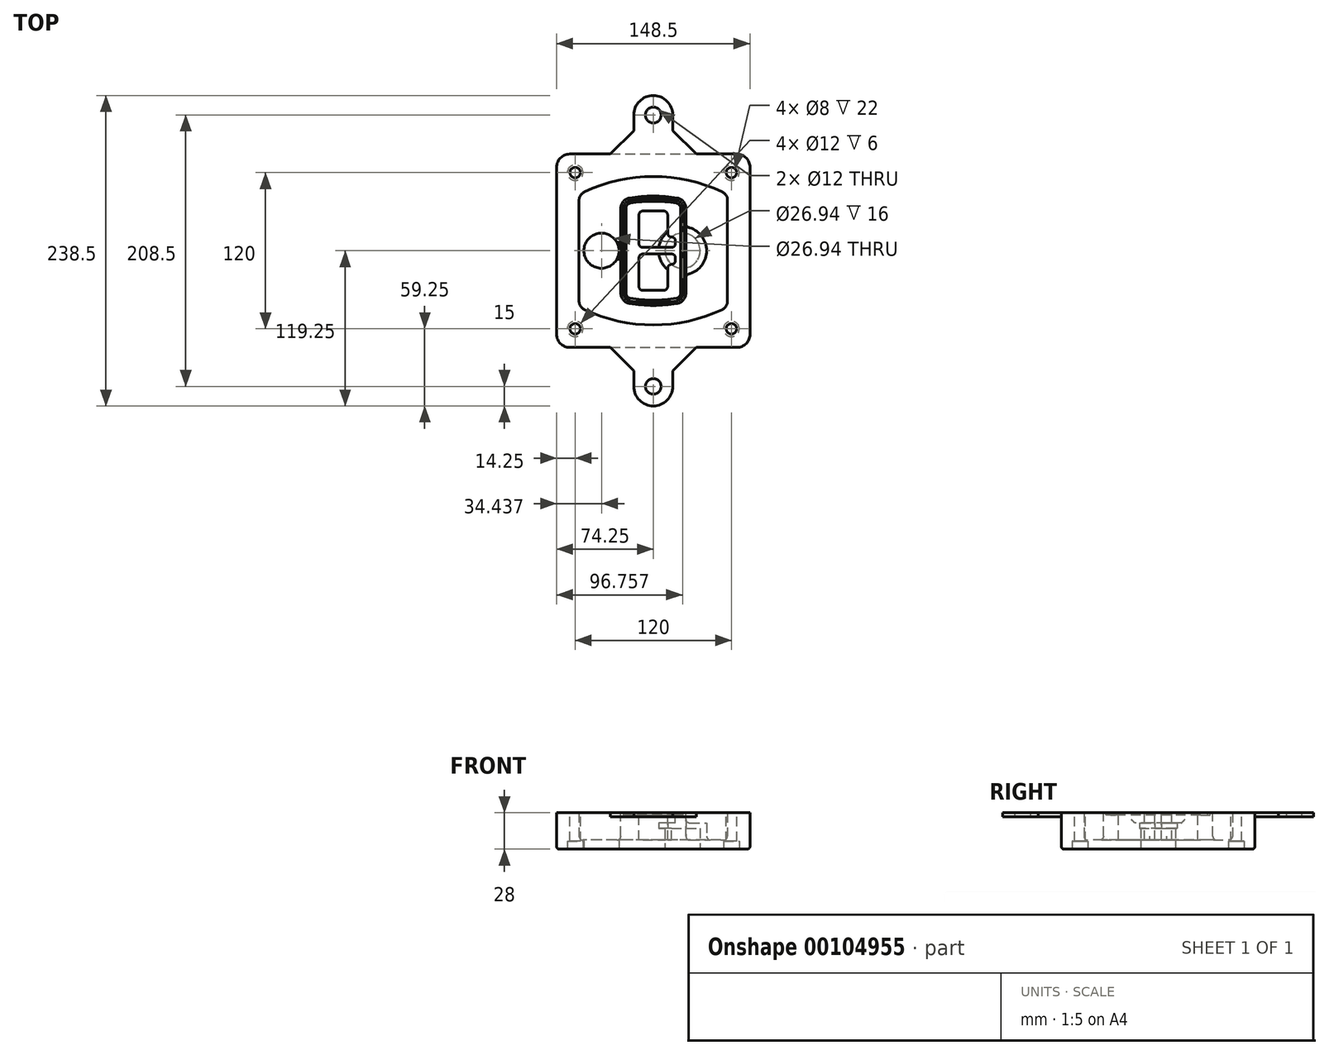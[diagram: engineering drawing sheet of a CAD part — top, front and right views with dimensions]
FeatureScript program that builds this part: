
annotation { "Feature Type Name" : "Feature", "Feature Type Description" : "" }
export const myFeature = defineFeature(function(context is Context, id is Id, definition is map)
    precondition{}
    {
        {
            var Q0;
            Q0=qCreatedBy(makeId("Top.planeOp"),FACE);
            var sketch = newSketch(context, id + "F0", { "sketchPlane" : qUnion([Q0])});
            skPoint(sketch, "E0.rect.middle", {"position": v(0, 0) * mm});
            skLineSegment(sketch, "E1.bottom", {"start": v(-64.25, -74.25) * mm, "end": v(64.25, -74.25) * mm});
            skLineSegment(sketch, "E1.top", {"start": v(-64.25, 74.25) * mm, "end": v(64.25, 74.25) * mm});
            skLineSegment(sketch, "E1.left", {"start": v(-74.25, -64.25) * mm, "end": v(-74.25, 64.25) * mm});
            skLineSegment(sketch, "E1.right", {"start": v(74.25, -64.25) * mm, "end": v(74.25, 64.25) * mm});
            skLineSegment(sketch, "E2", {"start": v(-74.25, 74.25) * mm, "end": v(74.25, -74.25) * mm, "construction": true});
            skLineSegment(sketch, "E3", {"start": v(74.25, 74.25) * mm, "end": v(-74.25, -74.25) * mm, "construction": true});
            skCircle(sketch, "E4", {"center": v(-60, 60) * mm, "radius": 4 * mm});
            skCircle(sketch, "E5", {"center": v(60, 60) * mm, "radius": 4 * mm});
            skCircle(sketch, "E6", {"center": v(60, -60) * mm, "radius": 4 * mm});
            skCircle(sketch, "E7", {"center": v(-60, -60) * mm, "radius": 4 * mm});
            skLineSegment(sketch, "E8", {"start": v(-60, 60) * mm, "end": v(60, 60) * mm, "construction": true});
            skLineSegment(sketch, "E9", {"start": v(60, 60) * mm, "end": v(60, -60) * mm, "construction": true});
            skLineSegment(sketch, "E10", {"start": v(60, -60) * mm, "end": v(-60, -60) * mm, "construction": true});
            skLineSegment(sketch, "E11", {"start": v(-60, -60) * mm, "end": v(-60, 60) * mm, "construction": true});
            skLineSegment(sketch, "E12", {"start": v(-60, 38.83) * mm, "end": v(-60, -38.83) * mm});
            skLineSegment(sketch, "E13", {"start": v(60, 38.83) * mm, "end": v(60, -38.83) * mm});
            skArc(sketch, "E14", {"start": v(54.26, 47.88) * mm, "mid": v(0, 60) * mm, "end": v(-54.26, 47.88) * mm});
            skArc(sketch, "E15", {"start": v(-54.26, -47.88) * mm, "mid": v(0, -60) * mm, "end": v(54.26, -47.88) * mm});
            skLineSegment(sketch, "E16", {"start": v(-60, 0) * mm, "end": v(60, 0) * mm, "construction": true});
            skPoint(sketch, "E17.visualSharp", {"position": v(-60, -45) * mm});
            skArc(sketch, "E17.filletArc", {"start": v(-60, -38.83) * mm, "mid": v(-58.44, -44.2) * mm, "end": v(-54.26, -47.88) * mm});
            skPoint(sketch, "E18.visualSharp", {"position": v(-60, 45) * mm});
            skArc(sketch, "E18.filletArc", {"start": v(-54.26, 47.88) * mm, "mid": v(-58.44, 44.2) * mm, "end": v(-60, 38.83) * mm});
            skPoint(sketch, "E19.visualSharp", {"position": v(60, 45) * mm});
            skArc(sketch, "E19.filletArc", {"start": v(60, 38.83) * mm, "mid": v(58.44, 44.2) * mm, "end": v(54.26, 47.88) * mm});
            skPoint(sketch, "E20.visualSharp", {"position": v(60, -45) * mm});
            skArc(sketch, "E20.filletArc", {"start": v(54.26, -47.88) * mm, "mid": v(58.44, -44.2) * mm, "end": v(60, -38.83) * mm});
            skPoint(sketch, "E21.visualSharp", {"position": v(-74.25, 74.25) * mm});
            skArc(sketch, "E21.filletArc", {"start": v(-64.25, 74.25) * mm, "mid": v(-71.32, 71.32) * mm, "end": v(-74.25, 64.25) * mm});
            skPoint(sketch, "E22.visualSharp", {"position": v(74.25, 74.25) * mm});
            skArc(sketch, "E22.filletArc", {"start": v(74.25, 64.25) * mm, "mid": v(71.32, 71.32) * mm, "end": v(64.25, 74.25) * mm});
            skPoint(sketch, "E23.visualSharp", {"position": v(74.25, -74.25) * mm});
            skArc(sketch, "E23.filletArc", {"start": v(64.25, -74.25) * mm, "mid": v(71.32, -71.32) * mm, "end": v(74.25, -64.25) * mm});
            skPoint(sketch, "E24.visualSharp", {"position": v(-74.25, -74.25) * mm});
            skArc(sketch, "E24.filletArc", {"start": v(-74.25, -64.25) * mm, "mid": v(-71.32, -71.32) * mm, "end": v(-64.25, -74.25) * mm});
            skArc(sketch, "E25.0", {"start": v(57, 38.83) * mm, "mid": v(55.9, 42.58) * mm, "end": v(52.98, 45.17) * mm});
            skLineSegment(sketch, "E25.1", {"start": v(57, 38.83) * mm, "end": v(57, -38.83) * mm});
            skArc(sketch, "E25.2", {"start": v(52.98, -45.17) * mm, "mid": v(55.9, -42.58) * mm, "end": v(57, -38.83) * mm});
            skArc(sketch, "E25.3", {"start": v(-52.98, -45.17) * mm, "mid": v(0, -57) * mm, "end": v(52.98, -45.17) * mm});
            skArc(sketch, "E25.4", {"start": v(-57, -38.83) * mm, "mid": v(-55.9, -42.58) * mm, "end": v(-52.98, -45.17) * mm});
            skArc(sketch, "E25.5", {"start": v(52.98, 45.17) * mm, "mid": v(0, 57) * mm, "end": v(-52.98, 45.17) * mm});
            skLineSegment(sketch, "E25.6", {"start": v(-57, 38.83) * mm, "end": v(-57, -38.83) * mm});
            skArc(sketch, "E25.7", {"start": v(-52.98, 45.17) * mm, "mid": v(-55.9, 42.58) * mm, "end": v(-57, 38.83) * mm});
            skArc(sketch, "E26.0", {"start": v(-55.96, 51.5) * mm, "mid": v(-61.82, 46.33) * mm, "end": v(-64, 38.83) * mm});
            skArc(sketch, "E26.1", {"start": v(55.96, 51.5) * mm, "mid": v(0, 64) * mm, "end": v(-55.96, 51.5) * mm});
            skArc(sketch, "E26.2", {"start": v(64, 38.83) * mm, "mid": v(61.82, 46.33) * mm, "end": v(55.96, 51.5) * mm});
            skLineSegment(sketch, "E26.3", {"start": v(64, 38.83) * mm, "end": v(64, -38.83) * mm});
            skArc(sketch, "E26.4", {"start": v(55.96, -51.5) * mm, "mid": v(61.82, -46.33) * mm, "end": v(64, -38.83) * mm});
            skLineSegment(sketch, "E26.5", {"start": v(-64, 38.83) * mm, "end": v(-64, -38.83) * mm});
            skArc(sketch, "E26.6", {"start": v(-55.96, -51.5) * mm, "mid": v(0, -64) * mm, "end": v(55.96, -51.5) * mm});
            skArc(sketch, "E26.7", {"start": v(-64, -38.83) * mm, "mid": v(-61.82, -46.33) * mm, "end": v(-55.96, -51.5) * mm});
            skSolve(sketch);
        }
        {
            var Q0;
            Q0=makeQuery(id+"F0.imprint","IMPRINT",FACE,{"disambiguationData":[TD([[makeQuery(id+"F0.imprint","IMPRINT",EDGE,{"derivedFrom":sQuery(id+"F0.wireOp",EDGE,"E1.bottom")}),1.0]])]});
            var Q1;
            Q1=makeQuery(id+"F0.imprint","IMPRINT",FACE,{"disambiguationData":[TD([[makeQuery(id+"F0.imprint","IMPRINT",EDGE,{"derivedFrom":sQuery(id+"F0.wireOp",EDGE,"E12")}),1.0]])]});
            var Q2;
            Q2=makeQuery(id+"F0.imprint","IMPRINT",FACE,{"disambiguationData":[TD([[makeQuery(id+"F0.imprint","IMPRINT",EDGE,{"derivedFrom":sQuery(id+"F0.wireOp",EDGE,"E25.0")}),1.0]])]});
            var Q3;
            Q3=makeQuery(id+"F0.imprint","IMPRINT",FACE,{"disambiguationData":[TD([[makeQuery(id+"F0.imprint","IMPRINT",EDGE,{"derivedFrom":sQuery(id+"F0.wireOp",EDGE,"E12")}),-1.0]])]});
            extrude(context, id + "F1", {"entities" : qUnion([Q0, Q1, Q2, Q3]), "oppositeDirection" : true, "depth" : 25 * mm});
        }
        {
            var Q0;
            Q0=makeQuery(id+"F0.imprint","IMPRINT",FACE,{"disambiguationData":[TD([[makeQuery(id+"F0.imprint","IMPRINT",EDGE,{"derivedFrom":sQuery(id+"F0.wireOp",EDGE,"E12")}),1.0]])]});
            extrude(context, id + "F2", {"entities" : qUnion([Q0]), "operationType" : NewBodyOperationType.ADD, "depth" : 3 * mm});
        }
        {
            var Q0;
            Q0=makeQuery(id+"F0.imprint","IMPRINT",FACE,{"disambiguationData":[TD([[makeQuery(id+"F0.imprint","IMPRINT",EDGE,{"derivedFrom":sQuery(id+"F0.wireOp",EDGE,"E25.0")}),1.0]])]});
            extrude(context, id + "F3", {"entities" : qUnion([Q0]), "operationType" : NewBodyOperationType.REMOVE, "oppositeDirection" : true, "depth" : 18 * mm});
        }
        {
            var Q0;
            Q0=makeQuery(id+"F2.opExtrude","CAP_FACE",FACE,{"disambiguationData":[OSD([sQuery(id+"F0.wireOp",EDGE,"E12"),sQuery(id+"F0.wireOp",EDGE,"E13"),sQuery(id+"F0.wireOp",EDGE,"E14"),sQuery(id+"F0.wireOp",EDGE,"E15"),sQuery(id+"F0.wireOp",EDGE,"E17.filletArc"),sQuery(id+"F0.wireOp",EDGE,"E18.filletArc"),sQuery(id+"F0.wireOp",EDGE,"E19.filletArc"),sQuery(id+"F0.wireOp",EDGE,"E20.filletArc"),sQuery(id+"F0.wireOp",EDGE,"E25.0"),sQuery(id+"F0.wireOp",EDGE,"E25.1"),sQuery(id+"F0.wireOp",EDGE,"E25.2"),sQuery(id+"F0.wireOp",EDGE,"E25.3"),sQuery(id+"F0.wireOp",EDGE,"E25.4"),sQuery(id+"F0.wireOp",EDGE,"E25.5"),sQuery(id+"F0.wireOp",EDGE,"E25.6"),sQuery(id+"F0.wireOp",EDGE,"E25.7")])],"isStart":false});
            var sketch = newSketch(context, id + "F4", { "sketchPlane" : qUnion([Q0])});
            skArc(sketch, "E27.0", {"start": v(-18.34, -40.45) * mm, "mid": v(0, -42) * mm, "end": v(18.34, -40.45) * mm});
            skArc(sketch, "E28.0", {"start": v(18.34, 40.45) * mm, "mid": v(0, 42) * mm, "end": v(-18.34, 40.45) * mm});
            skLineSegment(sketch, "E29", {"start": v(-25, 32.57) * mm, "end": v(-25, -32.57) * mm});
            skLineSegment(sketch, "E30", {"start": v(25, 32.57) * mm, "end": v(25, -32.57) * mm});
            skLineSegment(sketch, "E31", {"start": v(-25, 39.1) * mm, "end": v(25, 39.1) * mm, "construction": true});
            skLineSegment(sketch, "E32", {"start": v(-25, -39.1) * mm, "end": v(25, -39.1) * mm, "construction": true});
            skPoint(sketch, "E33.visualSharp", {"position": v(-25, 39.1) * mm});
            skArc(sketch, "E33.filletArc", {"start": v(-18.34, 40.45) * mm, "mid": v(-23.11, 37.73) * mm, "end": v(-25, 32.57) * mm});
            skPoint(sketch, "E34.visualSharp", {"position": v(25, 39.1) * mm});
            skArc(sketch, "E34.filletArc", {"start": v(25, 32.57) * mm, "mid": v(23.11, 37.73) * mm, "end": v(18.34, 40.45) * mm});
            skPoint(sketch, "E35.visualSharp", {"position": v(25, -39.1) * mm});
            skArc(sketch, "E35.filletArc", {"start": v(18.34, -40.45) * mm, "mid": v(23.11, -37.73) * mm, "end": v(25, -32.57) * mm});
            skPoint(sketch, "E36.visualSharp", {"position": v(-25, -39.1) * mm});
            skArc(sketch, "E36.filletArc", {"start": v(-25, -32.57) * mm, "mid": v(-23.11, -37.73) * mm, "end": v(-18.34, -40.45) * mm});
            skArc(sketch, "E37.0", {"start": v(52.98, 45.17) * mm, "mid": v(0, 57) * mm, "end": v(-52.98, 45.17) * mm});
            skArc(sketch, "E37.1", {"start": v(-52.98, 45.17) * mm, "mid": v(-55.9, 42.58) * mm, "end": v(-57, 38.83) * mm});
            skLineSegment(sketch, "E37.2", {"start": v(-57, 38.83) * mm, "end": v(-57, -38.83) * mm});
            skArc(sketch, "E37.3", {"start": v(-57, -38.83) * mm, "mid": v(-55.9, -42.58) * mm, "end": v(-52.98, -45.17) * mm});
            skArc(sketch, "E37.4", {"start": v(-52.98, -45.17) * mm, "mid": v(0, -57) * mm, "end": v(52.98, -45.17) * mm});
            skArc(sketch, "E37.5", {"start": v(52.98, -45.17) * mm, "mid": v(55.9, -42.58) * mm, "end": v(57, -38.83) * mm});
            skLineSegment(sketch, "E37.6", {"start": v(57, 38.83) * mm, "end": v(57, -38.83) * mm});
            skArc(sketch, "E37.7", {"start": v(57, 38.83) * mm, "mid": v(55.9, 42.58) * mm, "end": v(52.98, 45.17) * mm});
            skLineSegment(sketch, "E38.0", {"start": v(23, 32.57) * mm, "end": v(23, -32.57) * mm});
            skArc(sketch, "E38.1", {"start": v(18, -38.48) * mm, "mid": v(21.58, -36.44) * mm, "end": v(23, -32.57) * mm});
            skArc(sketch, "E38.2", {"start": v(-18, -38.48) * mm, "mid": v(0, -40) * mm, "end": v(18, -38.48) * mm});
            skArc(sketch, "E38.3", {"start": v(-23, -32.57) * mm, "mid": v(-21.58, -36.44) * mm, "end": v(-18, -38.48) * mm});
            skLineSegment(sketch, "E38.4", {"start": v(-23, 32.57) * mm, "end": v(-23, -32.57) * mm});
            skArc(sketch, "E38.5", {"start": v(23, 32.57) * mm, "mid": v(21.58, 36.44) * mm, "end": v(18, 38.48) * mm});
            skArc(sketch, "E38.6", {"start": v(-18, 38.48) * mm, "mid": v(-21.58, 36.44) * mm, "end": v(-23, 32.57) * mm});
            skArc(sketch, "E38.7", {"start": v(18, 38.48) * mm, "mid": v(0, 40) * mm, "end": v(-18, 38.48) * mm});
            skArc(sketch, "E39.0", {"start": v(21, 32.57) * mm, "mid": v(20.06, 35.15) * mm, "end": v(17.67, 36.5) * mm});
            skLineSegment(sketch, "E39.1", {"start": v(21, 32.57) * mm, "end": v(21, -32.57) * mm});
            skArc(sketch, "E39.2", {"start": v(17.67, -36.5) * mm, "mid": v(20.06, -35.15) * mm, "end": v(21, -32.57) * mm});
            skArc(sketch, "E39.3", {"start": v(-17.67, -36.5) * mm, "mid": v(0, -38) * mm, "end": v(17.67, -36.5) * mm});
            skArc(sketch, "E39.4", {"start": v(-21, -32.57) * mm, "mid": v(-20.06, -35.15) * mm, "end": v(-17.67, -36.5) * mm});
            skArc(sketch, "E39.5", {"start": v(17.67, 36.5) * mm, "mid": v(0, 38) * mm, "end": v(-17.67, 36.5) * mm});
            skLineSegment(sketch, "E39.6", {"start": v(-21, 32.57) * mm, "end": v(-21, -32.57) * mm});
            skArc(sketch, "E39.7", {"start": v(-17.67, 36.5) * mm, "mid": v(-20.06, 35.15) * mm, "end": v(-21, 32.57) * mm});
            skLineSegment(sketch, "E40", {"start": v(-25, 0) * mm, "end": v(25, 0) * mm, "construction": true});
            skLineSegment(sketch, "E41", {"start": v(-11, 5.5) * mm, "end": v(-11, 27.5) * mm});
            skLineSegment(sketch, "E42", {"start": v(-8, 30.5) * mm, "end": v(8, 30.5) * mm});
            skLineSegment(sketch, "E43", {"start": v(11, 27.5) * mm, "end": v(11, 13.5) * mm});
            skLineSegment(sketch, "E44", {"start": v(14, 10.5) * mm, "end": v(14, 10.5) * mm});
            skLineSegment(sketch, "E45", {"start": v(17, 7.5) * mm, "end": v(17, 5.5) * mm});
            skLineSegment(sketch, "E46", {"start": v(14, 2.5) * mm, "end": v(-8, 2.5) * mm});
            skPoint(sketch, "E47.visualSharp", {"position": v(-11, 30.5) * mm});
            skArc(sketch, "E47.filletArc", {"start": v(-8, 30.5) * mm, "mid": v(-10.12, 29.62) * mm, "end": v(-11, 27.5) * mm});
            skPoint(sketch, "E48.visualSharp", {"position": v(11, 30.5) * mm});
            skArc(sketch, "E48.filletArc", {"start": v(11, 27.5) * mm, "mid": v(10.12, 29.62) * mm, "end": v(8, 30.5) * mm});
            skPoint(sketch, "E49.visualSharp", {"position": v(11, 10.5) * mm});
            skArc(sketch, "E49.filletArc", {"start": v(11, 13.5) * mm, "mid": v(11.88, 11.38) * mm, "end": v(14, 10.5) * mm});
            skPoint(sketch, "E50.visualSharp", {"position": v(17, 10.5) * mm});
            skArc(sketch, "E50.filletArc", {"start": v(17, 7.5) * mm, "mid": v(16.12, 9.62) * mm, "end": v(14, 10.5) * mm});
            skPoint(sketch, "E51.visualSharp", {"position": v(17, 2.5) * mm});
            skArc(sketch, "E51.filletArc", {"start": v(14, 2.5) * mm, "mid": v(16.12, 3.38) * mm, "end": v(17, 5.5) * mm});
            skPoint(sketch, "E52.visualSharp", {"position": v(-11, 2.5) * mm});
            skArc(sketch, "E52.filletArc", {"start": v(-11, 5.5) * mm, "mid": v(-10.12, 3.38) * mm, "end": v(-8, 2.5) * mm});
            skLineSegment(sketch, "E53.0.MirrorCS", {"start": v(14, -2.5) * mm, "end": v(-8, -2.5) * mm});
            skArc(sketch, "E54.0.MirrorCS", {"start": v(-11, -5.5) * mm, "mid": v(-10.12, -3.38) * mm, "end": v(-8, -2.5) * mm});
            skLineSegment(sketch, "E55.0.MirrorCS", {"start": v(-11, -5.5) * mm, "end": v(-11, -27.5) * mm});
            skArc(sketch, "E56.0.MirrorCS", {"start": v(-8, -30.5) * mm, "mid": v(-10.12, -29.62) * mm, "end": v(-11, -27.5) * mm});
            skLineSegment(sketch, "E57.0.MirrorCS", {"start": v(-8, -30.5) * mm, "end": v(8, -30.5) * mm});
            skArc(sketch, "E58.0.MirrorCS", {"start": v(11, -27.5) * mm, "mid": v(10.12, -29.62) * mm, "end": v(8, -30.5) * mm});
            skLineSegment(sketch, "E59.0.MirrorCS", {"start": v(11, -27.5) * mm, "end": v(11, -13.5) * mm});
            skArc(sketch, "E60.0.MirrorCS", {"start": v(11, -13.5) * mm, "mid": v(11.88, -11.38) * mm, "end": v(14, -10.5) * mm});
            skArc(sketch, "E61.0.MirrorCS", {"start": v(17, -7.5) * mm, "mid": v(16.12, -9.62) * mm, "end": v(14, -10.5) * mm});
            skLineSegment(sketch, "E62.0.MirrorCS", {"start": v(17, -7.5) * mm, "end": v(17, -5.5) * mm});
            skArc(sketch, "E63.0.MirrorCS", {"start": v(14, -2.5) * mm, "mid": v(16.12, -3.38) * mm, "end": v(17, -5.5) * mm});
            skSolve(sketch);
        }
        {
            var Q0;
            Q0=makeQuery(id+"F4.imprint","IMPRINT",FACE,{"disambiguationData":[TD([[makeQuery(id+"F4.imprint","IMPRINT",EDGE,{"derivedFrom":sQuery(id+"F4.wireOp",EDGE,"E27.0")}),1.0]])]});
            var Q1;
            Q1=makeQuery(id+"F4.imprint","IMPRINT",FACE,{"disambiguationData":[TD([[makeQuery(id+"F4.imprint","IMPRINT",EDGE,{"derivedFrom":sQuery(id+"F4.wireOp",EDGE,"E38.0")}),-1.0]])]});
            var Q2;
            Q2=makeQuery(id+"F4.imprint","IMPRINT",FACE,{"disambiguationData":[TD([[makeQuery(id+"F4.imprint","IMPRINT",EDGE,{"derivedFrom":sQuery(id+"F4.wireOp",EDGE,"E39.0")}),1.0]])]});
            extrude(context, id + "F5", {"entities" : qUnion([Q0, Q1, Q2]), "operationType" : NewBodyOperationType.ADD, "endBound" : BoundingType.UP_TO_NEXT, "oppositeDirection" : true, "depth" : 25 * mm});
        }
        {
            var Q0;
            Q0=makeQuery(id+"F4.imprint","IMPRINT",FACE,{"disambiguationData":[TD([[makeQuery(id+"F4.imprint","IMPRINT",EDGE,{"derivedFrom":sQuery(id+"F4.wireOp",EDGE,"E38.0")}),-1.0]])]});
            extrude(context, id + "F6", {"entities" : qUnion([Q0]), "operationType" : NewBodyOperationType.REMOVE, "oppositeDirection" : true, "depth" : 2 * mm});
        }
        {
            var Q0;
            Q0=makeQuery(id+"F1.opExtrude","CAP_FACE",FACE,{"disambiguationData":[OSD([sQuery(id+"F0.wireOp",EDGE,"E1.bottom"),sQuery(id+"F0.wireOp",EDGE,"E1.top"),sQuery(id+"F0.wireOp",EDGE,"E1.left"),sQuery(id+"F0.wireOp",EDGE,"E1.right"),sQuery(id+"F0.wireOp",EDGE,"E4"),sQuery(id+"F0.wireOp",EDGE,"E5"),sQuery(id+"F0.wireOp",EDGE,"E6"),sQuery(id+"F0.wireOp",EDGE,"E7"),sQuery(id+"F0.wireOp",EDGE,"E21.filletArc"),sQuery(id+"F0.wireOp",EDGE,"E22.filletArc"),sQuery(id+"F0.wireOp",EDGE,"E23.filletArc"),sQuery(id+"F0.wireOp",EDGE,"E24.filletArc")])],"isStart":false});
            var sketch = newSketch(context, id + "F7", { "sketchPlane" : qUnion([Q0])});
            skCircle(sketch, "E64", {"center": v(22.5, 0) * mm, "radius": 13.47 * mm});
            skCircle(sketch, "E65", {"center": v(-39.81, 0) * mm, "radius": 13.47 * mm});
            skLineSegment(sketch, "E66", {"start": v(74.25, 0) * mm, "end": v(-74.25, 0) * mm});
            skCircle(sketch, "E67", {"center": v(22.5, 0) * mm, "radius": 18.47 * mm});
            skCircle(sketch, "E68", {"center": v(60, -60) * mm, "radius": 6 * mm});
            skCircle(sketch, "E69", {"center": v(-60, -60) * mm, "radius": 6 * mm});
            skCircle(sketch, "E70", {"center": v(-60, 60) * mm, "radius": 6 * mm});
            skCircle(sketch, "E71", {"center": v(60, 60) * mm, "radius": 6 * mm});
            skSolve(sketch);
        }
        {
            var Q0;
            {var subQ1=sQuery(id+"F7.wireOp",EDGE,"E66");var subQ4=sQuery(id+"F7.wireOp",EDGE,"E64");var subQ6=makeQuery(id+"F7.imprint","INTERSECT",VERTEX,{"disambiguationData":[OD(0.0)],"derivedFrom":[subQ4,subQ1]});Q0=makeQuery(id+"F7.imprint","IMPRINT",FACE,{"disambiguationData":[TD([[makeQuery(id+"F7.imprint","IMPRINT",EDGE,{"disambiguationData":[TD([[subQ6,-1.0]])],"derivedFrom":subQ4}),-1.0]])]});}
            var Q1;
            {var subQ0=sQuery(id+"F7.wireOp",EDGE,"E66");var subQ1=sQuery(id+"F7.wireOp",EDGE,"E64");var subQ3=makeQuery(id+"F7.imprint","INTERSECT",VERTEX,{"disambiguationData":[OD(0.0)],"derivedFrom":[subQ1,subQ0]});Q1=makeQuery(id+"F7.imprint","IMPRINT",FACE,{"disambiguationData":[TD([[makeQuery(id+"F7.imprint","IMPRINT",EDGE,{"disambiguationData":[TD([[subQ3,-1.0]])],"derivedFrom":subQ1}),1.0]])]});}
            var Q2;
            {var subQ0=sQuery(id+"F7.wireOp",EDGE,"E66");var subQ1=sQuery(id+"F7.wireOp",EDGE,"E64");var subQ3=makeQuery(id+"F7.imprint","INTERSECT",VERTEX,{"disambiguationData":[OD(0.0)],"derivedFrom":[subQ1,subQ0]});Q2=makeQuery(id+"F7.imprint","IMPRINT",FACE,{"disambiguationData":[TD([[makeQuery(id+"F7.imprint","IMPRINT",EDGE,{"disambiguationData":[TD([[subQ3,1.0]])],"derivedFrom":subQ1}),1.0]])]});}
            var Q3;
            {var subQ1=sQuery(id+"F7.wireOp",EDGE,"E66");var subQ4=sQuery(id+"F7.wireOp",EDGE,"E64");var subQ6=makeQuery(id+"F7.imprint","INTERSECT",VERTEX,{"disambiguationData":[OD(0.0)],"derivedFrom":[subQ4,subQ1]});Q3=makeQuery(id+"F7.imprint","IMPRINT",FACE,{"disambiguationData":[TD([[makeQuery(id+"F7.imprint","IMPRINT",EDGE,{"disambiguationData":[TD([[subQ6,1.0]])],"derivedFrom":subQ4}),-1.0]])]});}
            extrude(context, id + "F8", {"entities" : qUnion([Q0, Q1, Q2, Q3]), "operationType" : NewBodyOperationType.ADD, "oppositeDirection" : true, "depth" : 20 * mm});
        }
        {
            var Q0;
            {var subQ0=sQuery(id+"F7.wireOp",EDGE,"E66");var subQ1=sQuery(id+"F7.wireOp",EDGE,"E64");var subQ3=makeQuery(id+"F7.imprint","INTERSECT",VERTEX,{"disambiguationData":[OD(0.0)],"derivedFrom":[subQ1,subQ0]});Q0=makeQuery(id+"F7.imprint","IMPRINT",FACE,{"disambiguationData":[TD([[makeQuery(id+"F7.imprint","IMPRINT",EDGE,{"disambiguationData":[TD([[subQ3,-1.0]])],"derivedFrom":subQ1}),1.0]])]});}
            var Q1;
            {var subQ0=sQuery(id+"F7.wireOp",EDGE,"E66");var subQ1=sQuery(id+"F7.wireOp",EDGE,"E64");var subQ3=makeQuery(id+"F7.imprint","INTERSECT",VERTEX,{"disambiguationData":[OD(0.0)],"derivedFrom":[subQ1,subQ0]});Q1=makeQuery(id+"F7.imprint","IMPRINT",FACE,{"disambiguationData":[TD([[makeQuery(id+"F7.imprint","IMPRINT",EDGE,{"disambiguationData":[TD([[subQ3,1.0]])],"derivedFrom":subQ1}),1.0]])]});}
            extrude(context, id + "F9", {"entities" : qUnion([Q0, Q1]), "operationType" : NewBodyOperationType.REMOVE, "oppositeDirection" : true, "depth" : 16 * mm});
        }
        {
            var Q0;
            {var subQ0=sQuery(id+"F7.wireOp",EDGE,"E66");var subQ1=sQuery(id+"F7.wireOp",EDGE,"E65");var subQ3=makeQuery(id+"F7.imprint","INTERSECT",VERTEX,{"disambiguationData":[OD(0.0)],"derivedFrom":[subQ1,subQ0]});Q0=makeQuery(id+"F7.imprint","IMPRINT",FACE,{"disambiguationData":[TD([[makeQuery(id+"F7.imprint","IMPRINT",EDGE,{"disambiguationData":[TD([[subQ3,-1.0]])],"derivedFrom":subQ1}),1.0]])]});}
            var Q1;
            {var subQ0=sQuery(id+"F7.wireOp",EDGE,"E66");var subQ1=sQuery(id+"F7.wireOp",EDGE,"E65");var subQ3=makeQuery(id+"F7.imprint","INTERSECT",VERTEX,{"disambiguationData":[OD(0.0)],"derivedFrom":[subQ1,subQ0]});Q1=makeQuery(id+"F7.imprint","IMPRINT",FACE,{"disambiguationData":[TD([[makeQuery(id+"F7.imprint","IMPRINT",EDGE,{"disambiguationData":[TD([[subQ3,1.0]])],"derivedFrom":subQ1}),1.0]])]});}
            extrude(context, id + "F10", {"entities" : qUnion([Q0, Q1]), "operationType" : NewBodyOperationType.REMOVE, "oppositeDirection" : true, "depth" : 25 * mm});
        }
        {
            var Q0;
            Q0=makeQuery(id+"F7.imprint","IMPRINT",FACE,{"disambiguationData":[TD([[makeQuery(id+"F7.imprint","IMPRINT",EDGE,{"derivedFrom":sQuery(id+"F7.wireOp",EDGE,"E68")}),1.0]])]});
            var Q1;
            Q1=makeQuery(id+"F7.imprint","IMPRINT",FACE,{"disambiguationData":[TD([[makeQuery(id+"F7.imprint","IMPRINT",EDGE,{"derivedFrom":makeQuery(id+"F1.opExtrude","CAP_EDGE",EDGE,{"disambiguationData":[OSD([sQuery(id+"F0.wireOp",EDGE,"E5")])],"isStart":false})}),-1.0]])]});
            var Q2;
            Q2=makeQuery(id+"F7.imprint","IMPRINT",FACE,{"disambiguationData":[TD([[makeQuery(id+"F7.imprint","IMPRINT",EDGE,{"derivedFrom":sQuery(id+"F7.wireOp",EDGE,"E69")}),1.0]])]});
            var Q3;
            Q3=makeQuery(id+"F7.imprint","IMPRINT",FACE,{"disambiguationData":[TD([[makeQuery(id+"F7.imprint","IMPRINT",EDGE,{"derivedFrom":makeQuery(id+"F1.opExtrude","CAP_EDGE",EDGE,{"disambiguationData":[OSD([sQuery(id+"F0.wireOp",EDGE,"E4")])],"isStart":false})}),-1.0]])]});
            var Q4;
            Q4=makeQuery(id+"F7.imprint","IMPRINT",FACE,{"disambiguationData":[TD([[makeQuery(id+"F7.imprint","IMPRINT",EDGE,{"derivedFrom":sQuery(id+"F7.wireOp",EDGE,"E70")}),1.0]])]});
            var Q5;
            Q5=makeQuery(id+"F7.imprint","IMPRINT",FACE,{"disambiguationData":[TD([[makeQuery(id+"F7.imprint","IMPRINT",EDGE,{"derivedFrom":makeQuery(id+"F1.opExtrude","CAP_EDGE",EDGE,{"disambiguationData":[OSD([sQuery(id+"F0.wireOp",EDGE,"E7")])],"isStart":false})}),-1.0]])]});
            var Q6;
            Q6=makeQuery(id+"F7.imprint","IMPRINT",FACE,{"disambiguationData":[TD([[makeQuery(id+"F7.imprint","IMPRINT",EDGE,{"derivedFrom":sQuery(id+"F7.wireOp",EDGE,"E71")}),1.0]])]});
            var Q7;
            Q7=makeQuery(id+"F7.imprint","IMPRINT",FACE,{"disambiguationData":[TD([[makeQuery(id+"F7.imprint","IMPRINT",EDGE,{"derivedFrom":makeQuery(id+"F1.opExtrude","CAP_EDGE",EDGE,{"disambiguationData":[OSD([sQuery(id+"F0.wireOp",EDGE,"E6")])],"isStart":false})}),-1.0]])]});
            extrude(context, id + "F11", {"entities" : qUnion([Q0, Q1, Q2, Q3, Q4, Q5, Q6, Q7]), "operationType" : NewBodyOperationType.REMOVE, "oppositeDirection" : true, "depth" : 6 * mm});
        }
        {
            var Q0;
            Q0=makeQuery(id+"F9.boolean.opBoolean","COPY",FACE,{"derivedFrom":makeQuery(id+"F9.opExtrude","CAP_FACE",FACE,{"disambiguationData":[OSD([sQuery(id+"F7.wireOp",EDGE,"E64")])],"isStart":false})});
            var sketch = newSketch(context, id + "F12", { "sketchPlane" : qUnion([Q0])});
            skArc(sketch, "E72.0", {"start": v(11, 14.45) * mm, "mid": v(6.45, 9.13) * mm, "end": v(4.2, 2.5) * mm});
            skArc(sketch, "E72.1", {"start": v(4.2, -2.5) * mm, "mid": v(6.45, -9.13) * mm, "end": v(11, -14.45) * mm});
            skLineSegment(sketch, "E73", {"start": v(4.2, -2.5) * mm, "end": v(14, -2.5) * mm});
            skLineSegment(sketch, "E74.0", {"start": v(14, 2.5) * mm, "end": v(4.2, 2.5) * mm});
            skArc(sketch, "E74.1", {"start": v(14, 2.5) * mm, "mid": v(16.12, 3.38) * mm, "end": v(17, 5.5) * mm});
            skLineSegment(sketch, "E74.2", {"start": v(17, 7.5) * mm, "end": v(17, 5.5) * mm});
            skArc(sketch, "E74.3", {"start": v(17, 7.5) * mm, "mid": v(16.12, 9.62) * mm, "end": v(14, 10.5) * mm});
            skArc(sketch, "E74.4", {"start": v(11, 13.5) * mm, "mid": v(11.88, 11.38) * mm, "end": v(14, 10.5) * mm});
            skLineSegment(sketch, "E74.5", {"start": v(11, 14.45) * mm, "end": v(11, 13.5) * mm});
            skLineSegment(sketch, "E74.7", {"start": v(14, -2.5) * mm, "end": v(4.2, -2.5) * mm});
            skArc(sketch, "E74.8", {"start": v(14, -2.5) * mm, "mid": v(16.12, -3.38) * mm, "end": v(17, -5.5) * mm});
            skLineSegment(sketch, "E74.9", {"start": v(17, -7.5) * mm, "end": v(17, -5.5) * mm});
            skArc(sketch, "E74.10", {"start": v(17, -7.5) * mm, "mid": v(16.12, -9.62) * mm, "end": v(14, -10.5) * mm});
            skArc(sketch, "E74.11", {"start": v(11, -13.5) * mm, "mid": v(11.88, -11.38) * mm, "end": v(14, -10.5) * mm});
            skLineSegment(sketch, "E74.12", {"start": v(11, -14.45) * mm, "end": v(11, -13.5) * mm});
            skPoint(sketch, "E75.orphan", {"position": v(11, -27.5) * mm});
            skPoint(sketch, "E76.orphan", {"position": v(-8, -2.5) * mm});
            skPoint(sketch, "E77.orphan", {"position": v(-8, 2.5) * mm});
            skPoint(sketch, "E78.orphan", {"position": v(11, 27.5) * mm});
            skSolve(sketch);
        }
        {
            var Q0;
            {var subQ7=sQuery(id+"F12.wireOp",EDGE,"E72.0");var subQ14=sQuery(id+"F12.wireOp",EDGE,"E72.1");var subQ16=sQuery(id+"F12.wireOp",EDGE,"E74.1");var subQ18=sQuery(id+"F12.wireOp",EDGE,"E74.8");Q0=qUnion([makeQuery(id+"F12.imprint","IMPRINT",FACE,{"disambiguationData":[TD([[makeQuery(id+"F12.imprint","IMPRINT",EDGE,{"derivedFrom":subQ7}),1.0]])]}),makeQuery(id+"F12.imprint","IMPRINT",FACE,{"disambiguationData":[TD([[makeQuery(id+"F12.imprint","IMPRINT",EDGE,{"derivedFrom":subQ14}),1.0]])]}),makeQuery(id+"F12.imprint","IMPRINT",FACE,{"disambiguationData":[TD([[makeQuery(id+"F12.imprint","IMPRINT",EDGE,{"derivedFrom":subQ16}),1.0]])]}),makeQuery(id+"F12.imprint","IMPRINT",FACE,{"disambiguationData":[TD([[makeQuery(id+"F12.imprint","IMPRINT",EDGE,{"derivedFrom":subQ18}),-1.0]])]})]);}
            var Q1;
            Q1=makeQuery(id+"F5.boolean.opBoolean","SPLIT",FACE,{"disambiguationData":[TD([makeQuery(id+"F5.opExtrude","SWEPT_FACE",FACE,{"disambiguationData":[OSD([sQuery(id+"F4.wireOp",EDGE,"E41")])]})])],"derivedFrom":makeQuery(id+"F3.boolean.opBoolean","COPY",FACE,{"derivedFrom":makeQuery(id+"F3.opExtrude","CAP_FACE",FACE,{"disambiguationData":[OSD([sQuery(id+"F0.wireOp",EDGE,"E25.0"),sQuery(id+"F0.wireOp",EDGE,"E25.1"),sQuery(id+"F0.wireOp",EDGE,"E25.2"),sQuery(id+"F0.wireOp",EDGE,"E25.3"),sQuery(id+"F0.wireOp",EDGE,"E25.4"),sQuery(id+"F0.wireOp",EDGE,"E25.5"),sQuery(id+"F0.wireOp",EDGE,"E25.6"),sQuery(id+"F0.wireOp",EDGE,"E25.7")])],"isStart":false})})});
            extrude(context, id + "F13", {"entities" : qUnion([Q0]), "operationType" : NewBodyOperationType.REMOVE, "endBound" : BoundingType.UP_TO_SURFACE, "endBoundEntityFace" : qUnion([Q1]), "depth" : 25 * mm});
        }
        {
            var Q0;
            Q0=makeQuery(id+"F3.boolean.opBoolean","COPY",EDGE,{"derivedFrom":makeQuery(id+"F3.opExtrude","CAP_EDGE",EDGE,{"disambiguationData":[OSD([sQuery(id+"F0.wireOp",EDGE,"E25.6")])],"isStart":false})});
            var Q1;
            Q1=makeQuery(id+"F8.boolean.opBoolean","INTERSECT",EDGE,{"derivedFrom":[makeQuery(id+"F5.opExtrude","SWEPT_FACE",FACE,{"disambiguationData":[OSD([sQuery(id+"F4.wireOp",EDGE,"E30")])]}),makeQuery(id+"F8.opExtrude","CAP_FACE",FACE,{"disambiguationData":[OSD([sQuery(id+"F7.wireOp",EDGE,"E67")])],"isStart":false})]});
            var Q2;
            Q2=makeQuery(id+"F8.boolean.opBoolean","INTERSECT",EDGE,{"disambiguationData":[OD(1.0)],"derivedFrom":[makeQuery(id+"F5.opExtrude","SWEPT_FACE",FACE,{"disambiguationData":[OSD([sQuery(id+"F4.wireOp",EDGE,"E30")])]}),makeQuery(id+"F8.opExtrude","SWEPT_FACE",FACE,{"disambiguationData":[OSD([sQuery(id+"F7.wireOp",EDGE,"E67")])]})]});
            var Q3;
            {var subQ0=sQuery(id+"F4.wireOp",EDGE,"E30");Q3=makeQuery(id+"F8.boolean.opBoolean","SPLIT",EDGE,{"disambiguationData":[TD([makeQuery(id+"F5.opExtrude","SWEPT_FACE",FACE,{"disambiguationData":[OSD([sQuery(id+"F4.wireOp",EDGE,"E35.filletArc")])]})])],"derivedFrom":makeQuery(id+"F5.opExtrude","CAP_EDGE",EDGE,{"disambiguationData":[OSD([subQ0])],"isStart":false})});}
            var Q4;
            {var subQ0=sQuery(id+"F0.wireOp",EDGE,"E25.7");var subQ1=sQuery(id+"F0.wireOp",EDGE,"E25.1");var subQ2=sQuery(id+"F0.wireOp",EDGE,"E25.6");var subQ3=sQuery(id+"F0.wireOp",EDGE,"E25.5");var subQ4=sQuery(id+"F0.wireOp",EDGE,"E25.4");var subQ5=sQuery(id+"F0.wireOp",EDGE,"E25.0");var subQ6=sQuery(id+"F0.wireOp",EDGE,"E25.2");var subQ7=sQuery(id+"F0.wireOp",EDGE,"E25.3");Q4=makeQuery(id+"F8.boolean.opBoolean","INTERSECT",EDGE,{"derivedFrom":[makeQuery(id+"F5.boolean.opBoolean","SPLIT",FACE,{"disambiguationData":[TD([makeQuery(id+"F2.opExtrude","SWEPT_FACE",FACE,{"disambiguationData":[OSD([subQ5])]})])],"derivedFrom":makeQuery(id+"F3.boolean.opBoolean","COPY",FACE,{"derivedFrom":makeQuery(id+"F3.opExtrude","CAP_FACE",FACE,{"disambiguationData":[OSD([subQ5,subQ1,subQ6,subQ7,subQ4,subQ3,subQ2,subQ0])],"isStart":false})})}),makeQuery(id+"F8.opExtrude","SWEPT_FACE",FACE,{"disambiguationData":[OSD([sQuery(id+"F7.wireOp",EDGE,"E67")])]})]});}
            var Q5;
            Q5=makeQuery(id+"F8.boolean.opBoolean","INTERSECT",EDGE,{"disambiguationData":[OD(0.0)],"derivedFrom":[makeQuery(id+"F5.opExtrude","SWEPT_FACE",FACE,{"disambiguationData":[OSD([sQuery(id+"F4.wireOp",EDGE,"E30")])]}),makeQuery(id+"F8.opExtrude","SWEPT_FACE",FACE,{"disambiguationData":[OSD([sQuery(id+"F7.wireOp",EDGE,"E67")])]})]});
            fillet(context, id + "F14", {"entities" : qUnion([Q0, Q1, Q2, Q3, Q4, Q5]), "radius" : 3 * mm, "tangentPropagation" : true, "allowEdgeOverflow" : false});
        }
        {
            var Q0;
            Q0=makeQuery(id+"F1.opExtrude","CAP_EDGE",EDGE,{"disambiguationData":[OSD([sQuery(id+"F0.wireOp",EDGE,"E1.bottom")])],"isStart":false});
            fillet(context, id + "F15", {"entities" : qUnion([Q0]), "radius" : 2 * mm, "tangentPropagation" : true, "allowEdgeOverflow" : false});
        }
        {
            var Q0;
            {var subQ0=sQuery(id+"F0.wireOp",EDGE,"E22.filletArc");var subQ1=sQuery(id+"F0.wireOp",EDGE,"E7");var subQ2=sQuery(id+"F0.wireOp",EDGE,"E6");var subQ3=sQuery(id+"F0.wireOp",EDGE,"E5");var subQ4=sQuery(id+"F0.wireOp",EDGE,"E4");var subQ5=sQuery(id+"F0.wireOp",EDGE,"E1.bottom");var subQ6=sQuery(id+"F0.wireOp",EDGE,"E21.filletArc");var subQ7=sQuery(id+"F0.wireOp",EDGE,"E1.top");var subQ8=sQuery(id+"F0.wireOp",EDGE,"E1.left");var subQ9=sQuery(id+"F0.wireOp",EDGE,"E1.right");var subQ10=sQuery(id+"F0.wireOp",EDGE,"E23.filletArc");var subQ11=sQuery(id+"F0.wireOp",EDGE,"E24.filletArc");Q0=makeQuery(id+"F2.boolean.opBoolean","SPLIT",FACE,{"disambiguationData":[TD([makeQuery(id+"F1.opExtrude","SWEPT_FACE",FACE,{"disambiguationData":[OSD([subQ5])]})])],"derivedFrom":makeQuery(id+"F1.opExtrude","CAP_FACE",FACE,{"disambiguationData":[OSD([subQ5,subQ7,subQ8,subQ9,subQ4,subQ3,subQ2,subQ1,subQ6,subQ0,subQ10,subQ11])],"isStart":true})});}
            var sketch = newSketch(context, id + "F16", { "sketchPlane" : qUnion([Q0])});
            skLineSegment(sketch, "E79", {"start": v(0, 74.25) * mm, "end": v(0, 104.25) * mm, "construction": true});
            skCircle(sketch, "E80", {"center": v(0, 104.25) * mm, "radius": 6 * mm});
            skLineSegment(sketch, "E81", {"start": v(-33, 74.25) * mm, "end": v(-15, 92.25) * mm});
            skLineSegment(sketch, "E82", {"start": v(-15, 92.25) * mm, "end": v(-15, 104.25) * mm});
            skArc(sketch, "E83", {"start": v(15, 104.25) * mm, "mid": v(0, 119.25) * mm, "end": v(-15, 104.25) * mm});
            skLineSegment(sketch, "E84", {"start": v(15, 104.25) * mm, "end": v(15, 92.25) * mm});
            skLineSegment(sketch, "E85", {"start": v(15, 92.25) * mm, "end": v(33, 74.25) * mm});
            skLineSegment(sketch, "E86", {"start": v(74.25, 0) * mm, "end": v(-74.25, 0) * mm, "construction": true});
            skLineSegment(sketch, "E87.MirrorCS", {"start": v(-33, -74.25) * mm, "end": v(-15, -92.25) * mm});
            skLineSegment(sketch, "E88.MirrorCS", {"start": v(-15, -92.25) * mm, "end": v(-15, -104.25) * mm});
            skArc(sketch, "E89.MirrorCS", {"start": v(15, -104.25) * mm, "mid": v(0, -119.25) * mm, "end": v(-15, -104.25) * mm});
            skCircle(sketch, "E90.MirrorC", {"center": v(0, -104.25) * mm, "radius": 6 * mm});
            skLineSegment(sketch, "E91.MirrorCS", {"start": v(15, -104.25) * mm, "end": v(15, -92.25) * mm});
            skLineSegment(sketch, "E92.MirrorCS", {"start": v(15, -92.25) * mm, "end": v(33, -74.25) * mm});
            skSolve(sketch);
        }
        {
            var Q0;
            Q0=makeQuery(id+"F16.imprint","IMPRINT",FACE,{"disambiguationData":[TD([[makeQuery(id+"F16.imprint","IMPRINT",EDGE,{"derivedFrom":sQuery(id+"F16.wireOp",EDGE,"E80")}),-1.0]])]});
            var Q1;
            {var subQ0=sQuery(id+"F16.wireOp",EDGE,"E87.MirrorCS");Q1=makeQuery(id+"F16.imprint","IMPRINT",FACE,{"disambiguationData":[TD([[makeQuery(id+"F16.imprint","IMPRINT",EDGE,{"derivedFrom":subQ0}),1.0]])]});}
            var Q2;
            Q2=makeQuery(id+"F16.imprint","IMPRINT",FACE,{"disambiguationData":[TD([[makeQuery(id+"F16.imprint","IMPRINT",EDGE,{"derivedFrom":makeQuery(id+"F1.opExtrude","CAP_EDGE",EDGE,{"disambiguationData":[OSD([sQuery(id+"F0.wireOp",EDGE,"E1.left")])],"isStart":true})}),-1.0]])]});
            var Q3;
            Q3=makeQuery(id+"F2.opExtrude","CAP_FACE",FACE,{"disambiguationData":[OSD([sQuery(id+"F0.wireOp",EDGE,"E12"),sQuery(id+"F0.wireOp",EDGE,"E13"),sQuery(id+"F0.wireOp",EDGE,"E14"),sQuery(id+"F0.wireOp",EDGE,"E15"),sQuery(id+"F0.wireOp",EDGE,"E17.filletArc"),sQuery(id+"F0.wireOp",EDGE,"E18.filletArc"),sQuery(id+"F0.wireOp",EDGE,"E19.filletArc"),sQuery(id+"F0.wireOp",EDGE,"E20.filletArc"),sQuery(id+"F0.wireOp",EDGE,"E25.0"),sQuery(id+"F0.wireOp",EDGE,"E25.1"),sQuery(id+"F0.wireOp",EDGE,"E25.2"),sQuery(id+"F0.wireOp",EDGE,"E25.3"),sQuery(id+"F0.wireOp",EDGE,"E25.4"),sQuery(id+"F0.wireOp",EDGE,"E25.5"),sQuery(id+"F0.wireOp",EDGE,"E25.6"),sQuery(id+"F0.wireOp",EDGE,"E25.7")])],"isStart":false});
            extrude(context, id + "F17", {"entities" : qUnion([Q0, Q1, Q2]), "operationType" : NewBodyOperationType.ADD, "endBound" : BoundingType.UP_TO_SURFACE, "endBoundEntityFace" : qUnion([Q3]), "depth" : 25 * mm});
        }
    });
